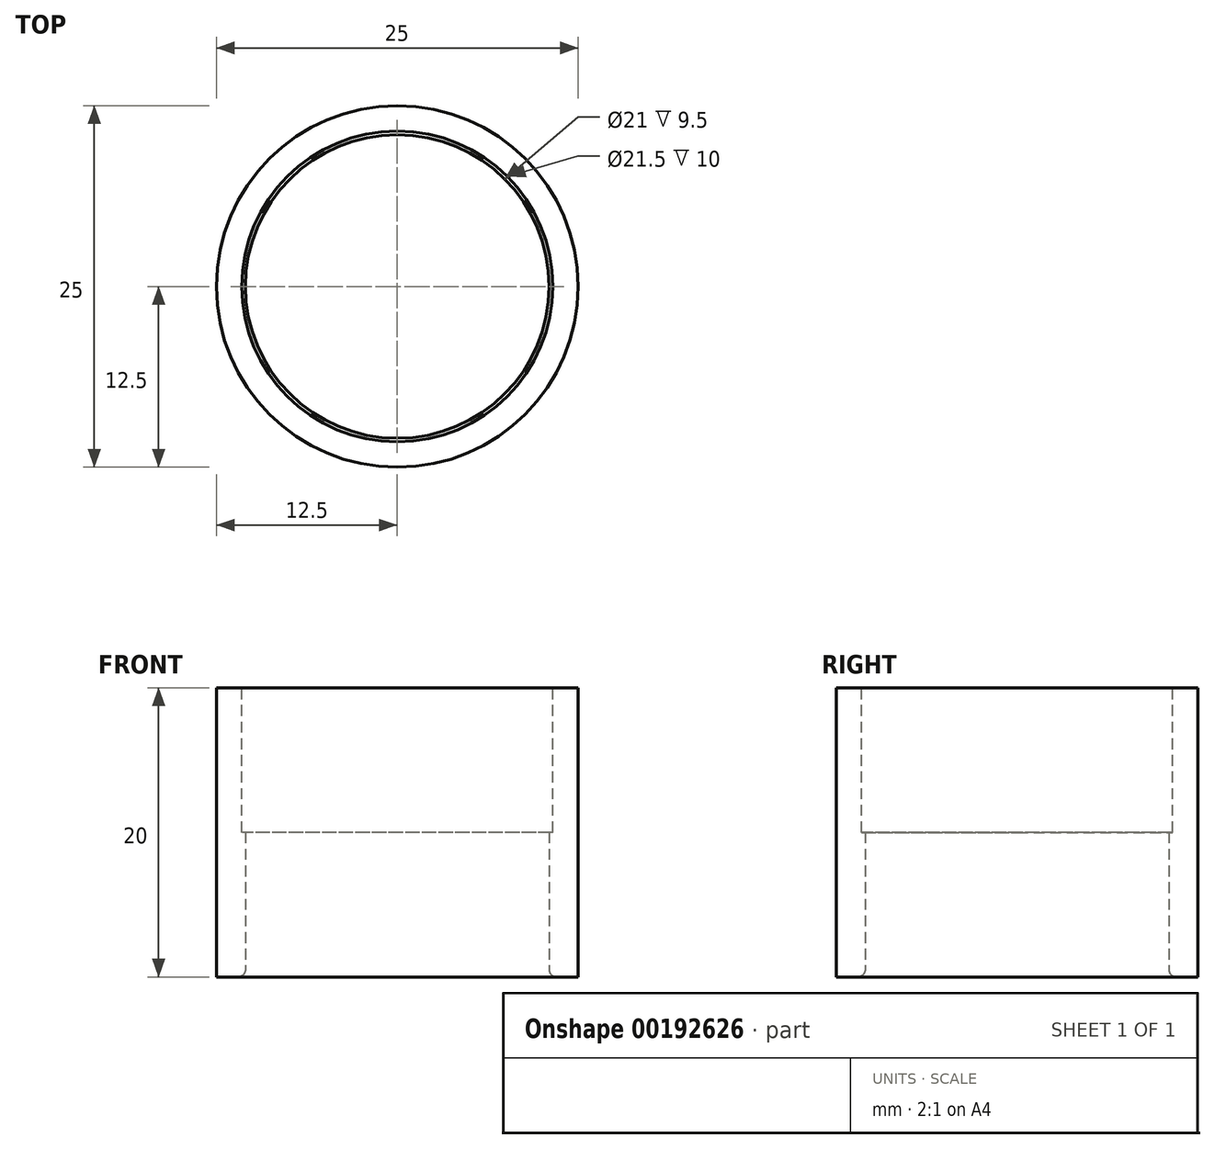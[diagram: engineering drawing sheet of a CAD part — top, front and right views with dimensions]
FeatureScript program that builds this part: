
annotation { "Feature Type Name" : "Feature", "Feature Type Description" : "" }
export const myFeature = defineFeature(function(context is Context, id is Id, definition is map)
    precondition{}
    {
        {
            var Q0;
            Q0=qCreatedBy(makeId("Top.planeOp"),FACE);
            cPlane(context, id + "F0", {"entities" : qUnion([Q0]), "cplaneType" : CPlaneType.OFFSET, "offset" : 36.5 * mm, "width" : 150 * mm, "height" : 150 * mm});
        }
        {
            var Q0;
            Q0=qCreatedBy(id+"F0.planeOp",FACE);
            var sketch = newSketch(context, id + "F1", { "sketchPlane" : qUnion([Q0])});
            skCircle(sketch, "E0", {"center": v(0, 0) * mm, "radius": 10.5 * mm});
            skCircle(sketch, "E1", {"center": v(0, 0) * mm, "radius": 12.5 * mm});
            skSolve(sketch);
        }
        {
            var Q0;
            Q0 = qSketchRegion(id + "F1", true);
            extrude(context, id + "F2", {"entities" : qUnion([Q0]), "depth" : 20 * mm});
        }
        {
            var Q0;
            Q0=makeQuery(id+"F2.opExtrude","CAP_FACE",FACE,{"disambiguationData":[OSD([sQuery(id+"F1.wireOp",EDGE,"E0"),sQuery(id+"F1.wireOp",EDGE,"E1")])],"isStart":false});
            var sketch = newSketch(context, id + "F3", { "sketchPlane" : qUnion([Q0])});
            skCircle(sketch, "E2", {"center": v(0, 0) * mm, "radius": 10.75 * mm});
            skSolve(sketch);
        }
        {
            var Q0;
            Q0 = qSketchRegion(id + "F3", true);
            extrude(context, id + "F4", {"entities" : qUnion([Q0]), "operationType" : NewBodyOperationType.REMOVE, "oppositeDirection" : true, "depth" : 10 * mm});
        }
        {
            var Q0;
            Q0=makeQuery(id+"F4.boolean.opBoolean","COPY",EDGE,{"derivedFrom":makeQuery(id+"F4.opExtrude","CAP_EDGE",EDGE,{"disambiguationData":[OSD([sQuery(id+"F3.wireOp",EDGE,"E2")])],"isStart":true})});
            var Q1;
            Q1=makeQuery(id+"F2.opExtrude","CAP_EDGE",EDGE,{"disambiguationData":[OSD([sQuery(id+"F1.wireOp",EDGE,"E0")])],"isStart":true});
            fillet(context, id + "F5", {"entities" : qUnion([Q0, Q1]), "radius" : .5 * mm, "tangentPropagation" : true, "allowEdgeOverflow" : false});
        }
    });
